# Revit family: Beacon Sconce
name_source: partatom
category: Lighting Fixtures
revit_build: Autodesk Revit 2017 (Build: 20190508_0315(x64)
units: mm (PartAtom-declared; Revit-internal decimal feet)

## family parameters
Cut with Voids When Loaded = No
Host = Face
Light Source = Yes
Part Type = Normal
Room Calculation Point = No
Round Connector Dimension = Use Diameter
Shared = No

## types (1)
- Beacon Sconce
    Canopy Width = 0"
    Color Filter = 16777215
    Cost = 399 $
    Default Elevation = 0"
    Description = The next generation of high-efficiency lighting is here in one innovative and visually-appealing package. The Beacon LED Sconce is an all-in-one wall sconce equipped with an integrated LED module that has the capacity to last for more than twenty years. Comes complete with a hand-blown Opal glass shade for a pleasing and diffuse glow. Expertly crafted and designed with beauty and utility as top priority, this low-profile fixture is ideal for both residential and commercial spaces where you want to install once and be done for good - no bulb replacement necessary. Assembled in our Portland, Ore. factory using ethically-sourced domestic and global components. A Schoolhouse Original.
    Dimming Lamp Color Temperature Shift = <None>
    Length = 6"
    Light Source Symbol Size = 12"
    Max Wattage = 14 W
    Primary Finishes = Natural Brass, True Black, Polished Nickel
    Product Material = Schoolhouse_Brass
    URL = https://www.schoolhouse.com
    Voltage = 120 V
    Width = 9 1/2"

## geometry (parser evidence)
native form markers: Sweep x3
no freeform markers — native parametric forms only
